# Revit family: IS_IdealrainPro_B9839_BIM_DE
name_source: partatom
category: Plumbing Fixtures
revit_build: Autodesk Revit MEP 2016 (Build: 20161004_0715(x64)
units: mm (PartAtom-declared; Revit-internal decimal feet)

## family parameters
Always vertical = No
Cut with Voids When Loaded = No
OmniClass Number = 23.45.05.14.17.17
OmniClass Title = Group Showers
Part Type = Normal
Room Calculation Point = No
Round Connector Dimension = Use Diameter
Shared = No
Work Plane-Based = No

## types (1)
- B9839AA IDEALRAIN PRO shower kit with single function 120mm handspray, 900mm slide rail
    Accessories = www.idealstandard.de\ersatzteile
    AreaUnits = millimeters
    AssetType = Fixed
    BIMObjectName = ISI_IdealStandard_ShowerMixers_IdealrainPro_B9839AA
    BIMobject category = Showers
    BOSUseNativeGeometries = 1
    BarCode = 3800861030157
    Brand = Ideal Standard
    Brand url = http://www.idealstandard.co.uk
    CodePerformance = 0
    Color = Chrome
    ConnectionType = Plumbing
    Cost = 0 $
    CurrencyUnit = €
    CurrentRevision = 1
    Date of publishing = 2017_11_21
    Description = B9839AA IDEALRAIN PRO shower kit with single function 120mm handspray, 900mm slide rail
    DurationUnit = year
    EAN code = https://3800861030157
    Edition number = 1
    ExpectedLife = 25
    FaucetType = pillar
    Features = IDEALRAIN PRO shower kit with single function 120mm handspray, 900mm slide rail
    Finish = Chrome
    IFC Classification = Sanitary Terminal
    IfcExportAs = IfcValveType
    IfcExportType = SHOWERMIXERS
    Installation instructions = http://www.idealstandard.de
    InstallationInstructions = www.idealstandard.de\produkte
    LinearUnits = millimeters
    MainColor = Chrome
    MaintenanceInformation = www.idealstandard.de\produkte
    Manufacturer name = Ideal Standard
    ManufacturerURL = www.idealstandard.com
    Material = Brass
    Material main = Brass
    Model = B9839AA
    ModelNumber = B9839AA
    ModelReference = B9839AA IDEALRAIN PRO shower kit with single function 120mm handspray, 900mm slide rail
    NBS Reference Code = 35-06-80
    NBS Reference Description = Shower Fittings Packages
    Name = ShowerMixers_IdealrainPro_B9839AA_IdealStandard
    NettWeight = 1,45 kg
    Nominal height = 900
    Nominal width = 153
    NominalDepth = 169 mm  [stored 0.554462 ft]
    NominalHeight = 900 mm  [stored 2.95276 ft]
    NominalLength = 169 mm  [stored 0.554462 ft]
    NominalWidth = 153 mm  [stored 0.501969 ft]
    OmniClass Code = 23-31 17 00
    OmniClass Description = Showers
    Product Guid = 56e9dafc-4551-47c3-ab90-a58a83c34d3c
    Product SKU = B9839
    Product data url = https://bimobject.com
    Product family = IDEALRAIN PRO
    Product group = Shower
    Product name = IDEALRAIN PRO shower kit with single function 120mm handspray, 900mm slide rail
    Product url = http://www.idealstandard.de
    ProductInformation = www.idealstandard.de/produkte
    QR code = http://bimobject.com
    Shape = Sculptured
    Size = 153x169x900 mm
    Space = Internal
    SpareParts = www.idealstandard.de/ersatzteile
    Technical description = http://www.idealstandard.de
    TestPressure = 10bar
    URL = www.idealstandard.com
    Uniclass 1.4 Code = L7214
    Uniclass 1.4 Description = Showers
    Uniclass 2.0 Code = PR-35-06-80
    Uniclass 2.0 Description = Shower Fittings Packages
    Uniclass 2015 Code = Pr_40_20_87_75
    Uniclass 2015 Name = Shower fittings package
    Uniclass2015Code = Pr_40_20_87_75
    Uniclass2015Title = Shower fittings package
    Uniclass2015Version = Products v1.1
    Version = 1
    VolumeUnits = Litres
    Weight Net (Kg) = 1.45
    WorkingPressure = 1-5 Bar

note: [stored X ft] marks values corroborated as IEEE doubles in the binary element streams (Revit-internal decimal feet)

## geometry (parser evidence)
native form markers: Blend x4, Sweep x1
no freeform markers — native parametric forms only
